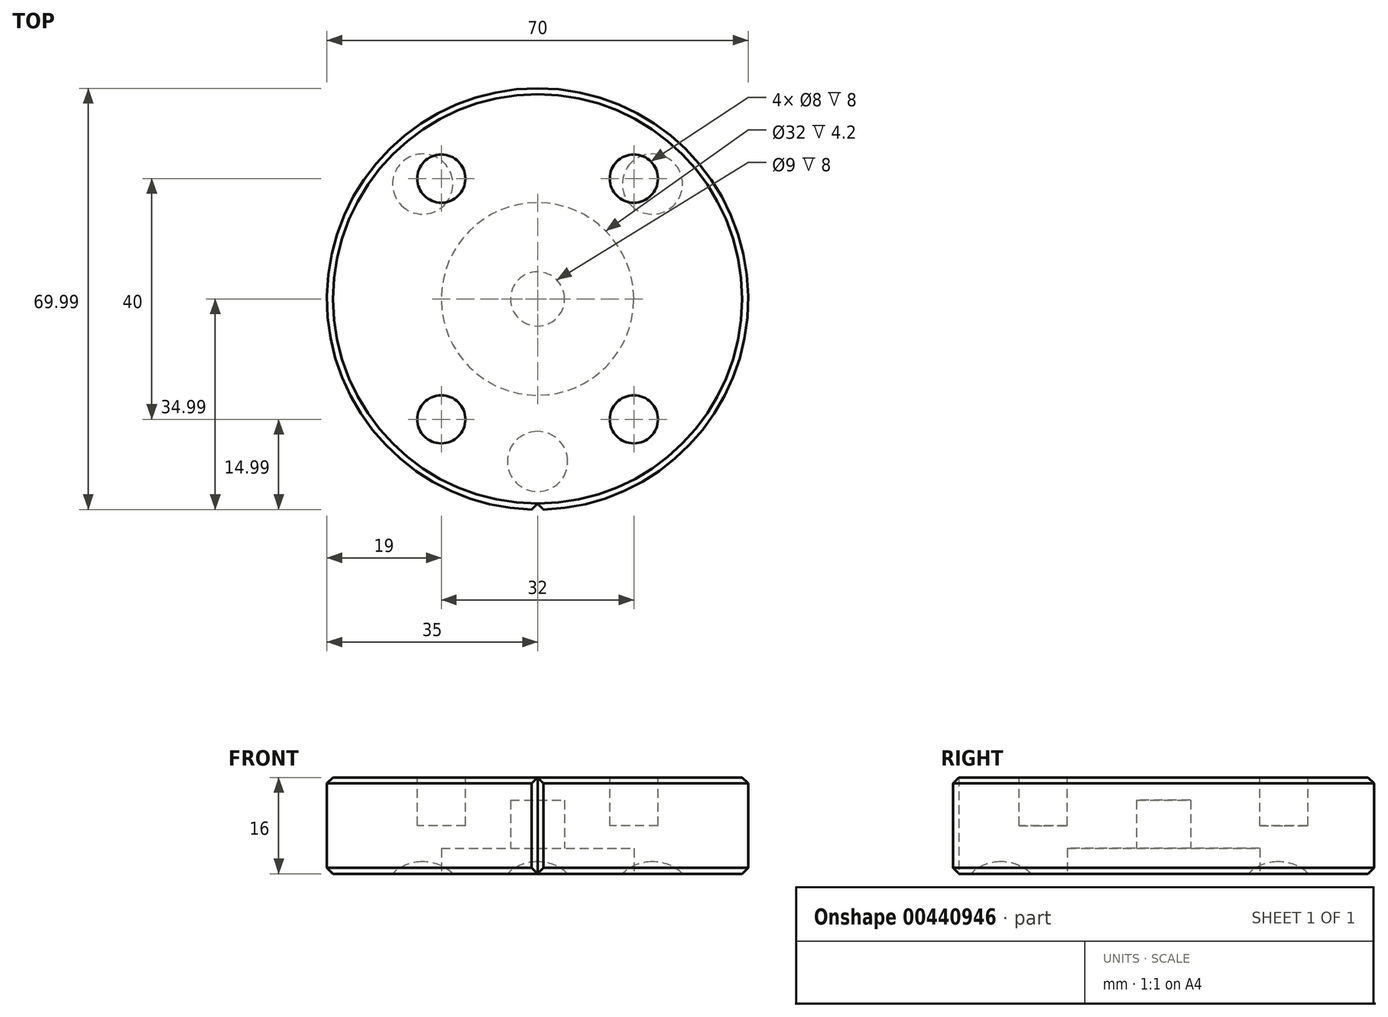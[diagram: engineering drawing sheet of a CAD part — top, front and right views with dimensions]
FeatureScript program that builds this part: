
annotation { "Feature Type Name" : "Feature", "Feature Type Description" : "" }
export const myFeature = defineFeature(function(context is Context, id is Id, definition is map)
    precondition{}
    {
        {
            var Q0;
            Q0=qCreatedBy(makeId("Top.planeOp"),FACE);
            var sketch = newSketch(context, id + "F0", { "sketchPlane" : qUnion([Q0])});
            skCircle(sketch, "E0", {"center": v(0, 0) * mm, "radius": 35 * mm});
            skLineSegment(sketch, "E1", {"start": v(0, 0) * mm, "end": v(0, -35) * mm, "construction": true});
            skLineSegment(sketch, "E2", {"start": v(0.99, -34.99) * mm, "end": v(0, -34) * mm});
            skLineSegment(sketch, "E3", {"start": v(0, -34) * mm, "end": v(-0.99, -34.99) * mm});
            skSolve(sketch);
        }
        {
            var Q0;
            Q0=qCreatedBy(makeId("Front.planeOp"),FACE);
            var sketch = newSketch(context, id + "F1", { "sketchPlane" : qUnion([Q0])});
            skLineSegment(sketch, "E4", {"start": v(0, 0) * mm, "end": v(0, 40) * mm, "construction": true});
            skSolve(sketch);
        }
        {
            var Q0;
            Q0=makeQuery(id+"F0.imprint","IMPRINT",FACE,{"disambiguationData":[TD([[makeQuery(id+"F0.imprint","IMPRINT",EDGE,{"derivedFrom":sQuery(id+"F0.wireOp",EDGE,"E0")}),1.0]])]});
            extrude(context, id + "F2", {"entities" : qUnion([Q0]), "depth" : 16 * mm});
        }
        {
            var Q0;
            Q0=makeQuery(id+"F2.opExtrude","CAP_FACE",FACE,{"disambiguationData":[OSD([sQuery(id+"F0.wireOp",EDGE,"E0")])],"isStart":false});
            var sketch = newSketch(context, id + "F3", { "sketchPlane" : qUnion([Q0])});
            skPoint(sketch, "E5", {"position": v(0, 0) * mm});
            skLineSegment(sketch, "E6.bottom", {"start": v(16, 20) * mm, "end": v(-16, 20) * mm, "construction": true});
            skLineSegment(sketch, "E6.top", {"start": v(16, -20) * mm, "end": v(-16, -20) * mm, "construction": true});
            skLineSegment(sketch, "E6.left", {"start": v(16, 20) * mm, "end": v(16, -20) * mm, "construction": true});
            skLineSegment(sketch, "E6.right", {"start": v(-16, 20) * mm, "end": v(-16, -20) * mm, "construction": true});
            skCircle(sketch, "E7", {"center": v(16, 20) * mm, "radius": 4 * mm});
            skCircle(sketch, "E8", {"center": v(16, -20) * mm, "radius": 4 * mm});
            skCircle(sketch, "E9", {"center": v(-16, -20) * mm, "radius": 4 * mm});
            skCircle(sketch, "E10", {"center": v(-16, 20) * mm, "radius": 4 * mm});
            skSolve(sketch);
        }
        {
            var Q0;
            Q0=makeQuery(id+"F2.opExtrude","CAP_FACE",FACE,{"disambiguationData":[OSD([sQuery(id+"F0.wireOp",EDGE,"E0")])],"isStart":true});
            var sketch = newSketch(context, id + "F4", { "sketchPlane" : qUnion([Q0])});
            skPoint(sketch, "E11", {"position": v(27, 0) * mm});
            skPoint(sketch, "E12.1.0", {"position": v(19.1, 19.1) * mm});
            skPoint(sketch, "E12.2.0", {"position": v(0, 27) * mm});
            skPoint(sketch, "E12.3.0", {"position": v(-19.1, 19.1) * mm});
            skPoint(sketch, "E12.4.0", {"position": v(-27, 0) * mm});
            skPoint(sketch, "E12.5.0", {"position": v(-19.1, -19.1) * mm});
            skPoint(sketch, "E12.6.0", {"position": v(0, -27) * mm});
            skPoint(sketch, "E12.7.0", {"position": v(19.1, -19.1) * mm});
            skCircle(sketch, "E13", {"center": v(0, 0) * mm, "radius": 16 * mm});
            skSolve(sketch);
        }
        {
            var Q0;
            Q0=makeQuery(id+"F4.imprint","IMPRINT",FACE,{"disambiguationData":[TD([[makeQuery(id+"F4.imprint","IMPRINT",EDGE,{"derivedFrom":sQuery(id+"F4.wireOp",EDGE,"E13")}),1.0]])]});
            extrude(context, id + "F5", {"entities" : qUnion([Q0]), "operationType" : NewBodyOperationType.REMOVE, "oppositeDirection" : true, "depth" : 4.2 * mm});
        }
        {
            var Q0;
            Q0=makeQuery(id+"F5.boolean.opBoolean","COPY",FACE,{"derivedFrom":makeQuery(id+"F5.opExtrude","CAP_FACE",FACE,{"disambiguationData":[OSD([sQuery(id+"F4.wireOp",EDGE,"E13")])],"isStart":false})});
            var sketch = newSketch(context, id + "F6", { "sketchPlane" : qUnion([Q0])});
            skCircle(sketch, "E14", {"center": v(0, 0) * mm, "radius": 4.5 * mm});
            skSolve(sketch);
        }
        {
            var Q0;
            Q0=makeQuery(id+"F6.imprint","IMPRINT",FACE,{"disambiguationData":[TD([[makeQuery(id+"F6.imprint","IMPRINT",EDGE,{"derivedFrom":sQuery(id+"F6.wireOp",EDGE,"E14")}),1.0]])]});
            extrude(context, id + "F7", {"entities" : qUnion([Q0]), "operationType" : NewBodyOperationType.REMOVE, "oppositeDirection" : true, "depth" : 8 * mm});
        }
        {
            var Q0;
            Q0=qCreatedBy(makeId("Right.planeOp"),FACE);
            var sketch = newSketch(context, id + "F8", { "sketchPlane" : qUnion([Q0])});
            skLineSegment(sketch, "E15", {"start": v(-32, 0) * mm, "end": v(-22, 0) * mm});
            skArc(sketch, "E16", {"start": v(-22, 0) * mm, "mid": v(-27, 2) * mm, "end": v(-32, 0) * mm});
            skLineSegment(sketch, "E17", {"start": v(-27, 0) * mm, "end": v(-27, 2) * mm});
            skSolve(sketch);
        }
        {
            var Q0;
            {var subQ3=sQuery(id+"F8.wireOp",EDGE,"E17");Q0=makeQuery(id+"F8.imprint","IMPRINT",FACE,{"disambiguationData":[TD([[makeQuery(id+"F8.imprint","IMPRINT",EDGE,{"derivedFrom":subQ3}),-1.0]])]});}
            var Q1;
            Q1=sQuery(id+"F8.wireOp",EDGE,"E17");
            revolve(context, id + "F9", {"entities" : qUnion([Q0]), "axis" : qUnion([Q1]), "revolveType" : RevolveType.FULL, "oppositeDirection" : true});
        }
        {
            var Q0;
            Q0=makeQuery(id+"F3.imprint","IMPRINT",FACE,{"disambiguationData":[TD([[makeQuery(id+"F3.imprint","IMPRINT",EDGE,{"derivedFrom":sQuery(id+"F3.wireOp",EDGE,"E10")}),1.0]])]});
            var Q1;
            Q1=makeQuery(id+"F3.imprint","IMPRINT",FACE,{"disambiguationData":[TD([[makeQuery(id+"F3.imprint","IMPRINT",EDGE,{"derivedFrom":sQuery(id+"F3.wireOp",EDGE,"E9")}),1.0]])]});
            var Q2;
            Q2=makeQuery(id+"F3.imprint","IMPRINT",FACE,{"disambiguationData":[TD([[makeQuery(id+"F3.imprint","IMPRINT",EDGE,{"derivedFrom":sQuery(id+"F3.wireOp",EDGE,"E7")}),1.0]])]});
            var Q3;
            Q3=makeQuery(id+"F3.imprint","IMPRINT",FACE,{"disambiguationData":[TD([[makeQuery(id+"F3.imprint","IMPRINT",EDGE,{"derivedFrom":sQuery(id+"F3.wireOp",EDGE,"E8")}),1.0]])]});
            extrude(context, id + "F10", {"entities" : qUnion([Q0, Q1, Q2, Q3]), "operationType" : NewBodyOperationType.REMOVE, "oppositeDirection" : true, "depth" : 8 * mm});
        }
        {
            var Q0;
            Q0=makeQuery(id+"F9.opRevolve","SWEPT_BODY",BODY,{"disambiguationData":[OSD([sQuery(id+"F8.wireOp",EDGE,"E15"),sQuery(id+"F8.wireOp",EDGE,"E16"),sQuery(id+"F8.wireOp",EDGE,"E17")])]});
            var Q1;
            Q1=sQuery(id+"F1.wireOp",EDGE,"E4");
            circularPattern(context, id + "F11", {"operationType" : NewBodyOperationType.REMOVE, "entities" : qUnion([Q0]), "axis" : qUnion([Q1]), "angle" : 135 * degree, "instanceCount" : 2, "isCentered" : true});
        }
        {
            var Q0;
            Q0=makeQuery(id+"F5.boolean.opBoolean","COPY",EDGE,{"derivedFrom":makeQuery(id+"F5.opExtrude","CAP_EDGE",EDGE,{"disambiguationData":[OSD([sQuery(id+"F4.wireOp",EDGE,"E13")])],"isStart":true})});
            var Q1;
            Q1=makeQuery(id+"F2.opExtrude","CAP_EDGE",EDGE,{"disambiguationData":[OSD([sQuery(id+"F0.wireOp",EDGE,"E0")])],"isStart":true});
            var Q2;
            Q2=makeQuery(id+"F2.opExtrude","CAP_EDGE",EDGE,{"disambiguationData":[OSD([sQuery(id+"F0.wireOp",EDGE,"E0")])],"isStart":false});
            var Q3;
            Q3=makeQuery(id+"F10.boolean.opBoolean","COPY",EDGE,{"derivedFrom":makeQuery(id+"F10.opExtrude","CAP_EDGE",EDGE,{"disambiguationData":[OSD([sQuery(id+"F3.wireOp",EDGE,"E8")])],"isStart":true})});
            var Q4;
            Q4=makeQuery(id+"F10.boolean.opBoolean","COPY",EDGE,{"derivedFrom":makeQuery(id+"F10.opExtrude","CAP_EDGE",EDGE,{"disambiguationData":[OSD([sQuery(id+"F3.wireOp",EDGE,"E9")])],"isStart":true})});
            var Q5;
            Q5=makeQuery(id+"F10.boolean.opBoolean","COPY",EDGE,{"derivedFrom":makeQuery(id+"F10.opExtrude","CAP_EDGE",EDGE,{"disambiguationData":[OSD([sQuery(id+"F3.wireOp",EDGE,"E10")])],"isStart":true})});
            var Q6;
            Q6=makeQuery(id+"F10.boolean.opBoolean","COPY",EDGE,{"derivedFrom":makeQuery(id+"F10.opExtrude","CAP_EDGE",EDGE,{"disambiguationData":[OSD([sQuery(id+"F3.wireOp",EDGE,"E7")])],"isStart":true})});
            chamfer(context, id + "F12", {"entities" : qUnion([Q0, Q1, Q2, Q3, Q4, Q5, Q6]), "width" : 1 * mm, "tangentPropagation" : true});
        }
        {
            var Q0;
            {var subQ0=sQuery(id+"F0.wireOp",EDGE,"E2");Q0=makeQuery(id+"F0.imprint","IMPRINT",FACE,{"disambiguationData":[TD([[makeQuery(id+"F0.imprint","IMPRINT",EDGE,{"derivedFrom":subQ0}),1.0]])]});}
            extrude(context, id + "F13", {"entities" : qUnion([Q0]), "operationType" : NewBodyOperationType.REMOVE, "depth" : 25 * mm, "offsetDistance" : 25 * mm});
        }
    });
